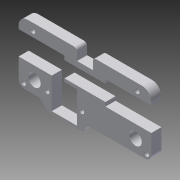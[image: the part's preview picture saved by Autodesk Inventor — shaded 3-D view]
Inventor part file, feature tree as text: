
AUTODESK INVENTOR PART (.ipt)
format: ipt  version: 2013 (Build 170138000, 138)  size: 179,712 bytes
history: native  units: mm
features: fillet x2, extrude x1, sketch x1
ambient origin geometry x8: Origin, YZ Plane, XZ Plane, XY Plane, X Axis, Y Axis, Z Axis, Center Point
bodies: Solid1 (feature_tree)
feature tree (4):
  extrude  "Extrusion1"  Depth=7.92mm TaperAngle=0.0deg
  fillet  "Fillet1"  Radius=10.0mm
  fillet  "Fillet2"  Radius=7.0mm
  sketch  "Sketch1"  dims[d0=39.0mm d1=84.0mm d18=3.0mm d19=3.0mm d20=3.0mm d21=3.0mm d23=9.0mm d24=9.0mm d25=3.0mm d26=3.0mm d27=26.0mm d28=5.0mm d29=42.0mm d31=20.0mm d32=5.0mm d33=1.5mm d34=3.0mm d35=3.0mm d36=3.0mm d37=3.0mm d38=11.0mm d40=7.92mm d41=6.4mm d42=0.0mm d43=10.0mm d44=7.0mm d45=39.5mm d46=7.92mm d47=8.0mm d48=10.0mm d49=10.0mm d50=8.0mm d51=8.0mm d52=2.5mm d53=2.5mm d54=29.0mm d55=26.0mm d56=29.0mm d57=26.0mm d58=16.0mm d59=37.0mm d60=2.0mm d61=4.0mm d62=6.0mm]
